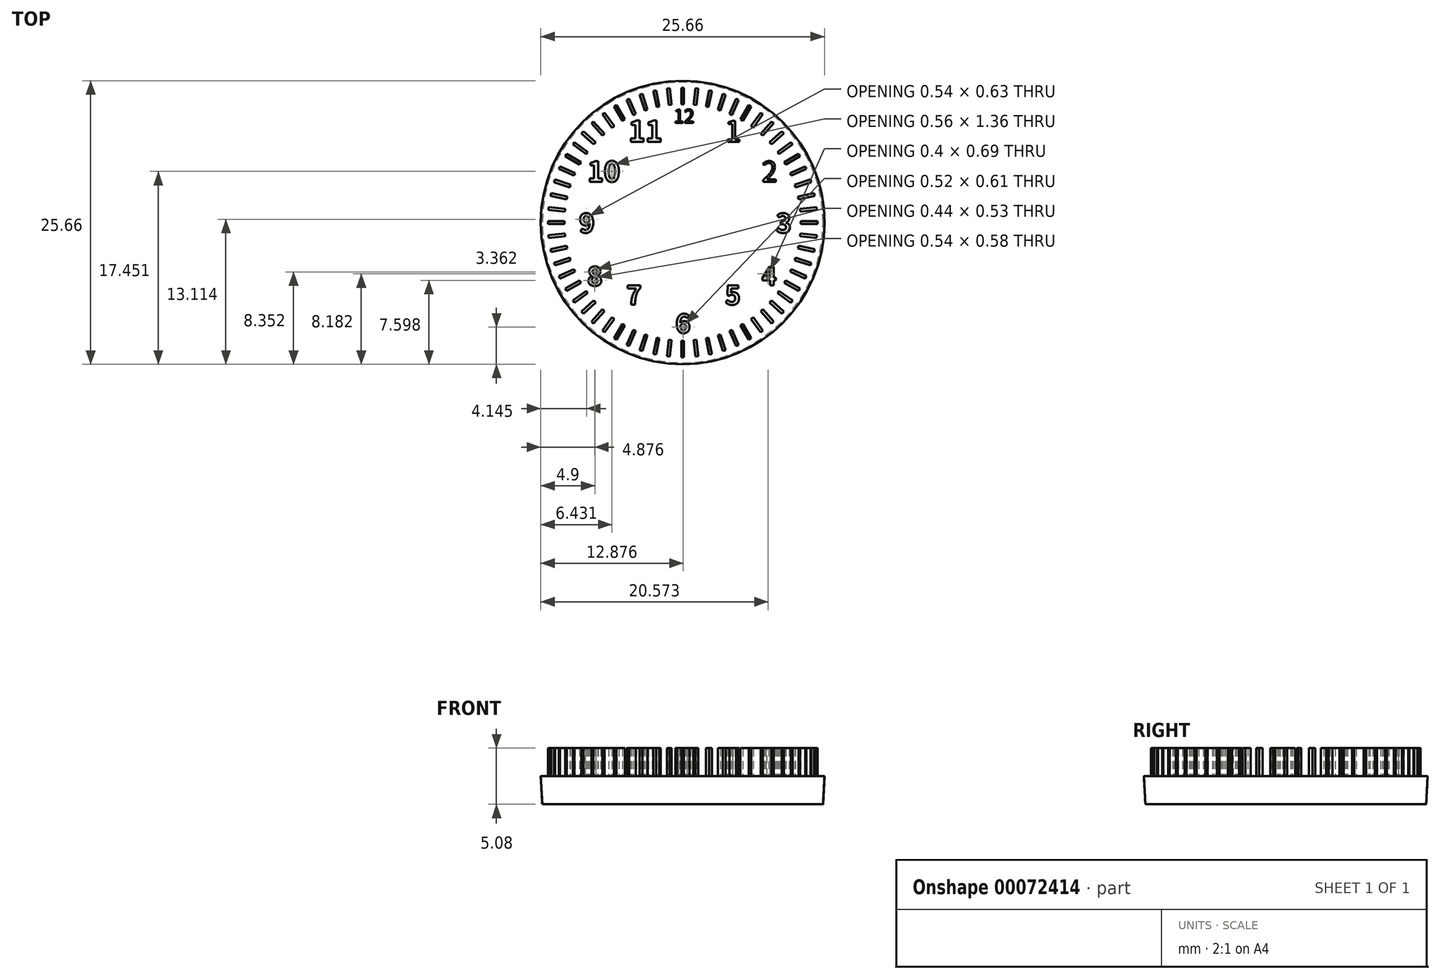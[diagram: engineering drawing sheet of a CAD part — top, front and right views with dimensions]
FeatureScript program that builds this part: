
annotation { "Feature Type Name" : "Feature", "Feature Type Description" : "" }
export const myFeature = defineFeature(function(context is Context, id is Id, definition is map)
    precondition{}
    {
        {
            var Q0;
            Q0=qCreatedBy(makeId("Top.planeOp"),FACE);
            var sketch = newSketch(context, id + "F0", { "sketchPlane" : qUnion([Q0])});
            skCircle(sketch, "E0", {"center": v(0, 0) * mm, "radius": 12.7 * mm});
            skLineSegment(sketch, "E1.rect.bottom", {"start": v(0.13, 12.2) * mm, "end": v(-0.13, 12.2) * mm});
            skLineSegment(sketch, "E1.rect.top", {"start": v(0.13, 10.7) * mm, "end": v(-0.13, 10.7) * mm});
            skLineSegment(sketch, "E1.rect.left", {"start": v(0.13, 12.2) * mm, "end": v(0.13, 10.7) * mm});
            skLineSegment(sketch, "E1.rect.right", {"start": v(-0.13, 12.2) * mm, "end": v(-0.13, 10.7) * mm});
            skPoint(sketch, "E1.rect.middle", {"position": v(0, 11.44) * mm});
            skSolve(sketch);
        }
        {
            var Q0;
            Q0=makeQuery(id+"F0.imprint","IMPRINT",FACE,{"disambiguationData":[TD([[makeQuery(id+"F0.imprint","IMPRINT",EDGE,{"derivedFrom":sQuery(id+"F0.wireOp",EDGE,"E0")}),1.0]])]});
            extrude(context, id + "F1", {"entities" : qUnion([Q0]), "depth" : 2.54 * mm, "hasDraft" : true, "draftAngle" : 3 * degree});
        }
        {
            var Q0;
            Q0=makeQuery(id+"F0.imprint","IMPRINT",FACE,{"disambiguationData":[TD([[makeQuery(id+"F0.imprint","IMPRINT",EDGE,{"derivedFrom":sQuery(id+"F0.wireOp",EDGE,"E1.rect.bottom")}),1.0]])]});
            extrude(context, id + "F2", {"entities" : qUnion([Q0]), "operationType" : NewBodyOperationType.ADD, "depth" : 5.08 * mm});
        }
        {
            var Q0;
            Q0=makeQuery(id+"F1.opExtrude","SWEPT_BODY",BODY,{"disambiguationData":[OSD([sQuery(id+"F0.wireOp",EDGE,"E0"),sQuery(id+"F0.wireOp",EDGE,"E1.rect.bottom"),sQuery(id+"F0.wireOp",EDGE,"E1.rect.top"),sQuery(id+"F0.wireOp",EDGE,"E1.rect.left"),sQuery(id+"F0.wireOp",EDGE,"E1.rect.right")])]});
            var Q1;
            Q1=makeQuery(id+"F1.opExtrude","CAP_EDGE",EDGE,{"disambiguationData":[OSD([sQuery(id+"F0.wireOp",EDGE,"E0")])],"isStart":false});
            circularPattern(context, id + "F3", {"entities" : qUnion([Q0]), "axis" : qUnion([Q1]), "angle" : 6 * degree, "instanceCount" : 60});
        }
        {
            var Q0;
            Q0=makeQuery(id+"F3.opPattern","COPY",FACE,{"derivedFrom":makeQuery(id+"F1.opExtrude","CAP_FACE",FACE,{"disambiguationData":[OSD([sQuery(id+"F0.wireOp",EDGE,"E0"),sQuery(id+"F0.wireOp",EDGE,"E1.rect.bottom"),sQuery(id+"F0.wireOp",EDGE,"E1.rect.top"),sQuery(id+"F0.wireOp",EDGE,"E1.rect.left"),sQuery(id+"F0.wireOp",EDGE,"E1.rect.right"),sQuery(id+"F0.wireOp",EDGE,"3f156231-64e9-476c-97a6-e4f65410bd27.sketch_text.stroke-0"),sQuery(id+"F0.wireOp",EDGE,"3f156231-64e9-476c-97a6-e4f65410bd27.sketch_text.stroke-1"),sQuery(id+"F0.wireOp",EDGE,"3f156231-64e9-476c-97a6-e4f65410bd27.sketch_text.stroke-2"),sQuery(id+"F0.wireOp",EDGE,"3f156231-64e9-476c-97a6-e4f65410bd27.sketch_text.stroke-3"),sQuery(id+"F0.wireOp",EDGE,"3f156231-64e9-476c-97a6-e4f65410bd27.sketch_text.stroke-4"),sQuery(id+"F0.wireOp",EDGE,"3f156231-64e9-476c-97a6-e4f65410bd27.sketch_text.stroke-5"),sQuery(id+"F0.wireOp",EDGE,"3f156231-64e9-476c-97a6-e4f65410bd27.sketch_text.stroke-6"),sQuery(id+"F0.wireOp",EDGE,"3f156231-64e9-476c-97a6-e4f65410bd27.sketch_text.stroke-7"),sQuery(id+"F0.wireOp",EDGE,"3f156231-64e9-476c-97a6-e4f65410bd27.sketch_text.stroke-8"),sQuery(id+"F0.wireOp",EDGE,"3f156231-64e9-476c-97a6-e4f65410bd27.sketch_text.stroke-9"),sQuery(id+"F0.wireOp",EDGE,"3f156231-64e9-476c-97a6-e4f65410bd27.sketch_text.stroke-10"),sQuery(id+"F0.wireOp",EDGE,"3f156231-64e9-476c-97a6-e4f65410bd27.sketch_text.stroke-11"),sQuery(id+"F0.wireOp",EDGE,"3f156231-64e9-476c-97a6-e4f65410bd27.sketch_text.stroke-12"),sQuery(id+"F0.wireOp",EDGE,"3f156231-64e9-476c-97a6-e4f65410bd27.sketch_text.stroke-13"),sQuery(id+"F0.wireOp",EDGE,"3f156231-64e9-476c-97a6-e4f65410bd27.sketch_text.stroke-14"),sQuery(id+"F0.wireOp",EDGE,"3f156231-64e9-476c-97a6-e4f65410bd27.sketch_text.stroke-15"),sQuery(id+"F0.wireOp",EDGE,"3f156231-64e9-476c-97a6-e4f65410bd27.sketch_text.stroke-16"),sQuery(id+"F0.wireOp",EDGE,"3f156231-64e9-476c-97a6-e4f65410bd27.sketch_text.stroke-17"),sQuery(id+"F0.wireOp",EDGE,"3f156231-64e9-476c-97a6-e4f65410bd27.sketch_text.stroke-18"),sQuery(id+"F0.wireOp",EDGE,"3f156231-64e9-476c-97a6-e4f65410bd27.sketch_text.stroke-19"),sQuery(id+"F0.wireOp",EDGE,"3f156231-64e9-476c-97a6-e4f65410bd27.sketch_text.stroke-20"),sQuery(id+"F0.wireOp",EDGE,"3f156231-64e9-476c-97a6-e4f65410bd27.sketch_text.stroke-21"),sQuery(id+"F0.wireOp",EDGE,"3f156231-64e9-476c-97a6-e4f65410bd27.sketch_text.stroke-22")])],"isStart":false}),"instanceName":"3"});
            var sketch = newSketch(context, id + "F4", { "sketchPlane" : qUnion([Q0])});
            skText(sketch, "E2", { "text": "1", "fontName": "NotoSansCJKkr-Regular.otf"});
            skText(sketch, "E3", { "text": "2", "fontName": "NotoSansCJKkr-Regular.otf"});
            skText(sketch, "E4", { "text": "3", "fontName": "NotoSansCJKsc-Bold.otf"});
            skText(sketch, "E5", { "text": "4", "fontName": "NotoSansCJKsc-Bold.otf"});
            skText(sketch, "E6", { "text": "5", "fontName": "NotoSansCJKsc-Bold.otf"});
            skText(sketch, "E7", { "text": "6", "fontName": "NotoSansCJKsc-Bold.otf"});
            skText(sketch, "E8", { "text": "7", "fontName": "NotoSansCJKsc-Bold.otf"});
            skText(sketch, "E9", { "text": "8", "fontName": "NotoSansCJKsc-Bold.otf"});
            skText(sketch, "E10", { "text": "9", "fontName": "NotoSansCJKsc-Bold.otf"});
            skText(sketch, "E11", { "text": "10", "fontName": "NotoSansCJKsc-Bold.otf"});
            skText(sketch, "E12", { "text": "11", "fontName": "NotoSansCJKsc-Bold.otf"});
            skText(sketch, "E13", { "text": "12", "fontName": "NotoSansCJKsc-Regular.otf"});
            skCircle(sketch, "E14", {"center": v(0, 0) * mm, "radius": 12.7 * mm});
            const initialGuessF4  = {"E2": [0.00384, 0.00731, 1, 0, 0.00187], "E3": [0.00717, 0.00369, 1, 0, 0.00181], "E4": [0.00844, -0.00093, 1, 0, 0.00171], "E5": [0.00717, -0.00568, 1, 0, 0.00163], "E6": [0.00384, -0.00744, 1, 0, 0.0017], "E7": [-0.00065, -0.01, 1, 0, 0.00167], "E8": [-0.0051, -0.00744, 1, 0, 0.0017], "E9": [-0.00863, -0.00573, 1, 0, 0.00168], "E10": [-0.00937, -0.00093, 1, 0, 0.00171], "E11": [-0.00862, 0.00369, 1, 0, 0.00181], "E12": [-0.0049, 0.00731, 1, 0, 0.00187], "E13": [-0.0008, 0.00901, 1, 0, 0.0012]};
            skSetInitialGuess(sketch, initialGuessF4);
            skSolve(sketch);
        }
        {
            var Q0;
            Q0=makeQuery(id+"F4.imprint","IMPRINT",FACE,{"disambiguationData":[TD([[makeQuery(id+"F4.imprint","IMPRINT",EDGE,{"derivedFrom":sQuery(id+"F4.wireOp",EDGE,"E11.sketch_text.stroke-0")}),1.0]])]});
            var Q1;
            Q1=makeQuery(id+"F4.imprint","IMPRINT",FACE,{"disambiguationData":[TD([[makeQuery(id+"F4.imprint","IMPRINT",EDGE,{"derivedFrom":sQuery(id+"F4.wireOp",EDGE,"E9.sketch_text.stroke-0")}),1.0]])]});
            var Q2;
            Q2=makeQuery(id+"F4.imprint","IMPRINT",FACE,{"disambiguationData":[TD([[makeQuery(id+"F4.imprint","IMPRINT",EDGE,{"derivedFrom":sQuery(id+"F4.wireOp",EDGE,"E4.sketch_text.stroke-0")}),1.0]])]});
            var Q3;
            Q3=makeQuery(id+"F4.imprint","IMPRINT",FACE,{"disambiguationData":[TD([[makeQuery(id+"F4.imprint","IMPRINT",EDGE,{"derivedFrom":sQuery(id+"F4.wireOp",EDGE,"E12.sketch_text.stroke-11")}),1.0]])]});
            var Q4;
            Q4=makeQuery(id+"F4.imprint","IMPRINT",FACE,{"disambiguationData":[TD([[makeQuery(id+"F4.imprint","IMPRINT",EDGE,{"derivedFrom":sQuery(id+"F4.wireOp",EDGE,"E13.sketch_text.stroke-11")}),1.0]])]});
            var Q5;
            Q5=makeQuery(id+"F4.imprint","IMPRINT",FACE,{"disambiguationData":[TD([[makeQuery(id+"F4.imprint","IMPRINT",EDGE,{"derivedFrom":sQuery(id+"F4.wireOp",EDGE,"E6.sketch_text.stroke-0")}),1.0]])]});
            var Q6;
            Q6=makeQuery(id+"F4.imprint","IMPRINT",FACE,{"disambiguationData":[TD([[makeQuery(id+"F4.imprint","IMPRINT",EDGE,{"derivedFrom":sQuery(id+"F4.wireOp",EDGE,"E3.sketch_text.stroke-0")}),1.0]])]});
            var Q7;
            Q7=makeQuery(id+"F4.imprint","IMPRINT",FACE,{"disambiguationData":[TD([[makeQuery(id+"F4.imprint","IMPRINT",EDGE,{"derivedFrom":sQuery(id+"F4.wireOp",EDGE,"E12.sketch_text.stroke-0")}),1.0]])]});
            var Q8;
            Q8=makeQuery(id+"F4.imprint","IMPRINT",FACE,{"disambiguationData":[TD([[makeQuery(id+"F4.imprint","IMPRINT",EDGE,{"derivedFrom":sQuery(id+"F4.wireOp",EDGE,"E13.sketch_text.stroke-0")}),1.0]])]});
            var Q9;
            Q9=makeQuery(id+"F4.imprint","IMPRINT",FACE,{"disambiguationData":[TD([[makeQuery(id+"F4.imprint","IMPRINT",EDGE,{"derivedFrom":sQuery(id+"F4.wireOp",EDGE,"E7.sketch_text.stroke-0")}),1.0]])]});
            var Q10;
            Q10=makeQuery(id+"F4.imprint","IMPRINT",FACE,{"disambiguationData":[TD([[makeQuery(id+"F4.imprint","IMPRINT",EDGE,{"derivedFrom":sQuery(id+"F4.wireOp",EDGE,"E8.sketch_text.stroke-0")}),1.0]])]});
            var Q11;
            Q11=makeQuery(id+"F4.imprint","IMPRINT",FACE,{"disambiguationData":[TD([[makeQuery(id+"F4.imprint","IMPRINT",EDGE,{"derivedFrom":sQuery(id+"F4.wireOp",EDGE,"E10.sketch_text.stroke-0")}),1.0]])]});
            var Q12;
            Q12=makeQuery(id+"F4.imprint","IMPRINT",FACE,{"disambiguationData":[TD([[makeQuery(id+"F4.imprint","IMPRINT",EDGE,{"derivedFrom":sQuery(id+"F4.wireOp",EDGE,"E2.sketch_text.stroke-0")}),1.0]])]});
            var Q13;
            Q13=makeQuery(id+"F4.imprint","IMPRINT",FACE,{"disambiguationData":[TD([[makeQuery(id+"F4.imprint","IMPRINT",EDGE,{"derivedFrom":sQuery(id+"F4.wireOp",EDGE,"E5.sketch_text.stroke-0")}),1.0]])]});
            var Q14;
            Q14=makeQuery(id+"F4.imprint","IMPRINT",FACE,{"disambiguationData":[TD([[makeQuery(id+"F4.imprint","IMPRINT",EDGE,{"derivedFrom":sQuery(id+"F4.wireOp",EDGE,"E11.sketch_text.stroke-11")}),1.0]])]});
            extrude(context, id + "F5", {"entities" : qUnion([Q0, Q1, Q2, Q3, Q4, Q5, Q6, Q7, Q8, Q9, Q10, Q11, Q12, Q13, Q14]), "depth" : 2.54 * mm});
        }
    });
